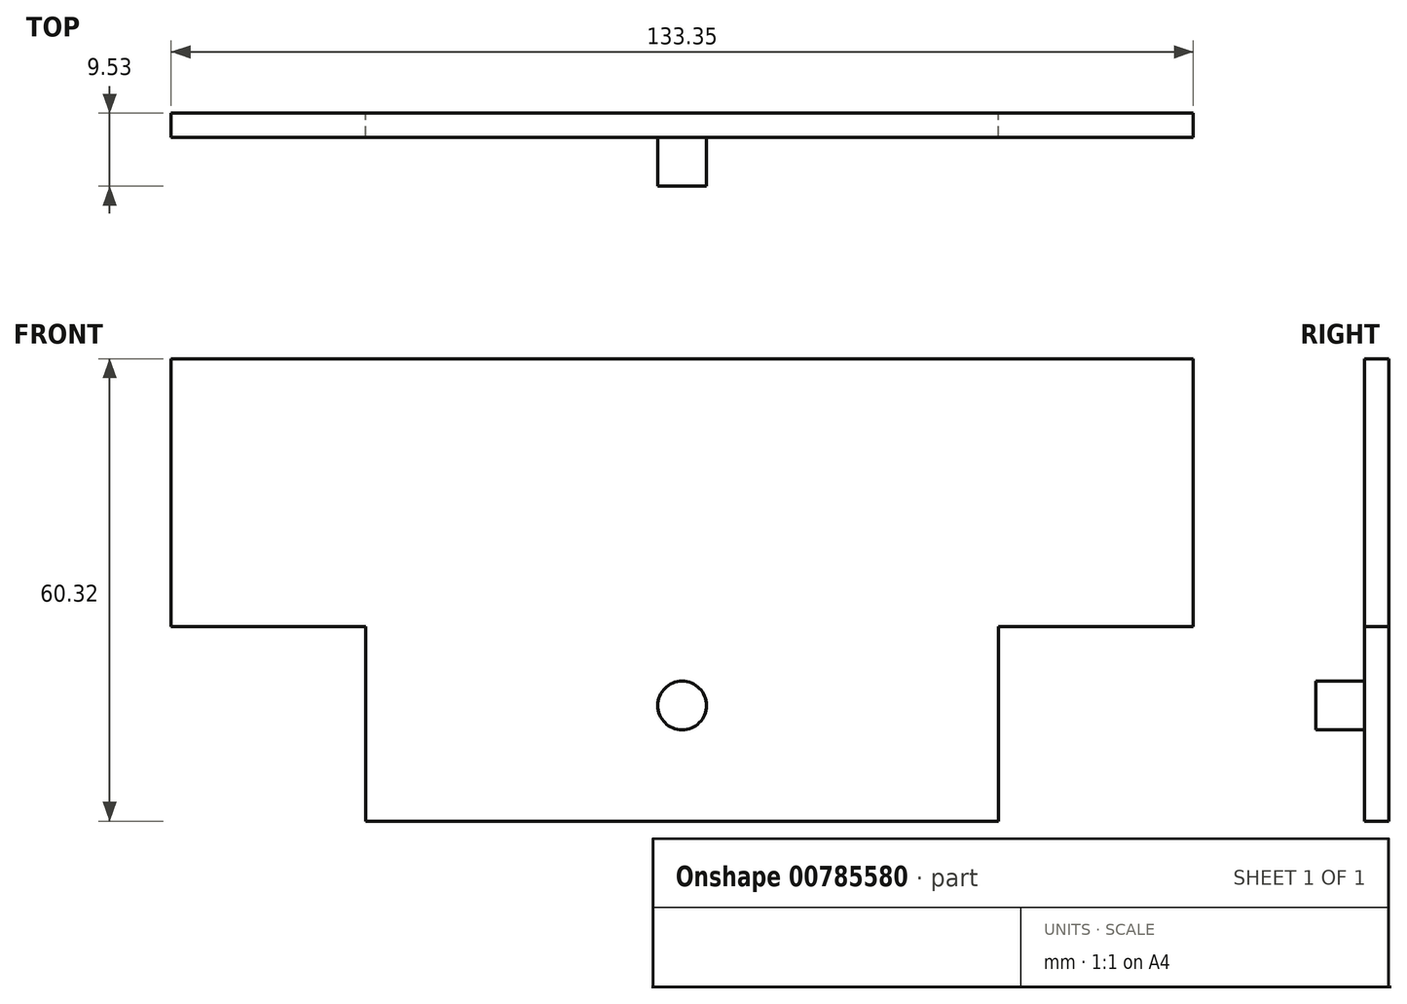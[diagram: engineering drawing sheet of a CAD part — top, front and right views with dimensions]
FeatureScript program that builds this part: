
annotation { "Feature Type Name" : "Feature", "Feature Type Description" : "" }
export const myFeature = defineFeature(function(context is Context, id is Id, definition is map)
    precondition{}
    {
        {
            var Q0;
            Q0=qCreatedBy(makeId("Front.planeOp"),FACE);
            var sketch = newSketch(context, id + "F0", { "sketchPlane" : qUnion([Q0])});
            skLineSegment(sketch, "E0.bottom", {"start": v(63.07, 30.16) * mm, "end": v(-70.28, 30.16) * mm});
            skLineSegment(sketch, "E0.top", {"start": v(63.07, -30.16) * mm, "end": v(-70.28, -30.16) * mm});
            skLineSegment(sketch, "E0.left", {"start": v(63.07, 30.16) * mm, "end": v(63.07, -30.16) * mm});
            skLineSegment(sketch, "E0.right", {"start": v(-70.28, 30.16) * mm, "end": v(-70.28, -30.16) * mm});
            skPoint(sketch, "E0.middle", {"position": v(-3.6, 0) * mm});
            skCircle(sketch, "E1", {"center": v(-3.6, -15.07) * mm, "radius": 3.18 * mm});
            skLineSegment(sketch, "E2.bottom", {"start": v(-70.28, -30.16) * mm, "end": v(-44.88, -30.16) * mm});
            skLineSegment(sketch, "E2.top", {"start": v(-70.28, -4.76) * mm, "end": v(-44.88, -4.76) * mm});
            skLineSegment(sketch, "E2.left", {"start": v(-70.28, -30.16) * mm, "end": v(-70.28, -4.76) * mm});
            skLineSegment(sketch, "E2.right", {"start": v(-44.88, -30.16) * mm, "end": v(-44.88, -4.76) * mm});
            skLineSegment(sketch, "E3.bottom", {"start": v(63.07, -30.16) * mm, "end": v(37.67, -30.16) * mm});
            skLineSegment(sketch, "E3.top", {"start": v(63.07, -4.76) * mm, "end": v(37.67, -4.76) * mm});
            skLineSegment(sketch, "E3.left", {"start": v(63.07, -30.16) * mm, "end": v(63.07, -4.76) * mm});
            skLineSegment(sketch, "E3.right", {"start": v(37.67, -30.16) * mm, "end": v(37.67, -4.76) * mm});
            skSolve(sketch);
        }
        {
            var Q0;
            {var subQ1=sQuery(id+"F0.wireOp",EDGE,"E0.bottom");Q0=makeQuery(id+"F0.imprint","IMPRINT",FACE,{"disambiguationData":[TD([[makeQuery(id+"F0.imprint","IMPRINT",EDGE,{"derivedFrom":subQ1}),1.0]])]});}
            extrude(context, id + "F1", {"entities" : qUnion([Q0]), "depth" : 3.17 * mm, "offsetDistance" : 25.4 * mm});
        }
        {
            var Q0;
            Q0=makeQuery(id+"F0.imprint","IMPRINT",FACE,{"disambiguationData":[TD([[makeQuery(id+"F0.imprint","IMPRINT",EDGE,{"derivedFrom":sQuery(id+"F0.wireOp",EDGE,"E1")}),1.0]])]});
            extrude(context, id + "F2", {"entities" : qUnion([Q0]), "operationType" : NewBodyOperationType.ADD, "depth" : 9.52 * mm, "offsetDistance" : 25.4 * mm});
        }
    });
